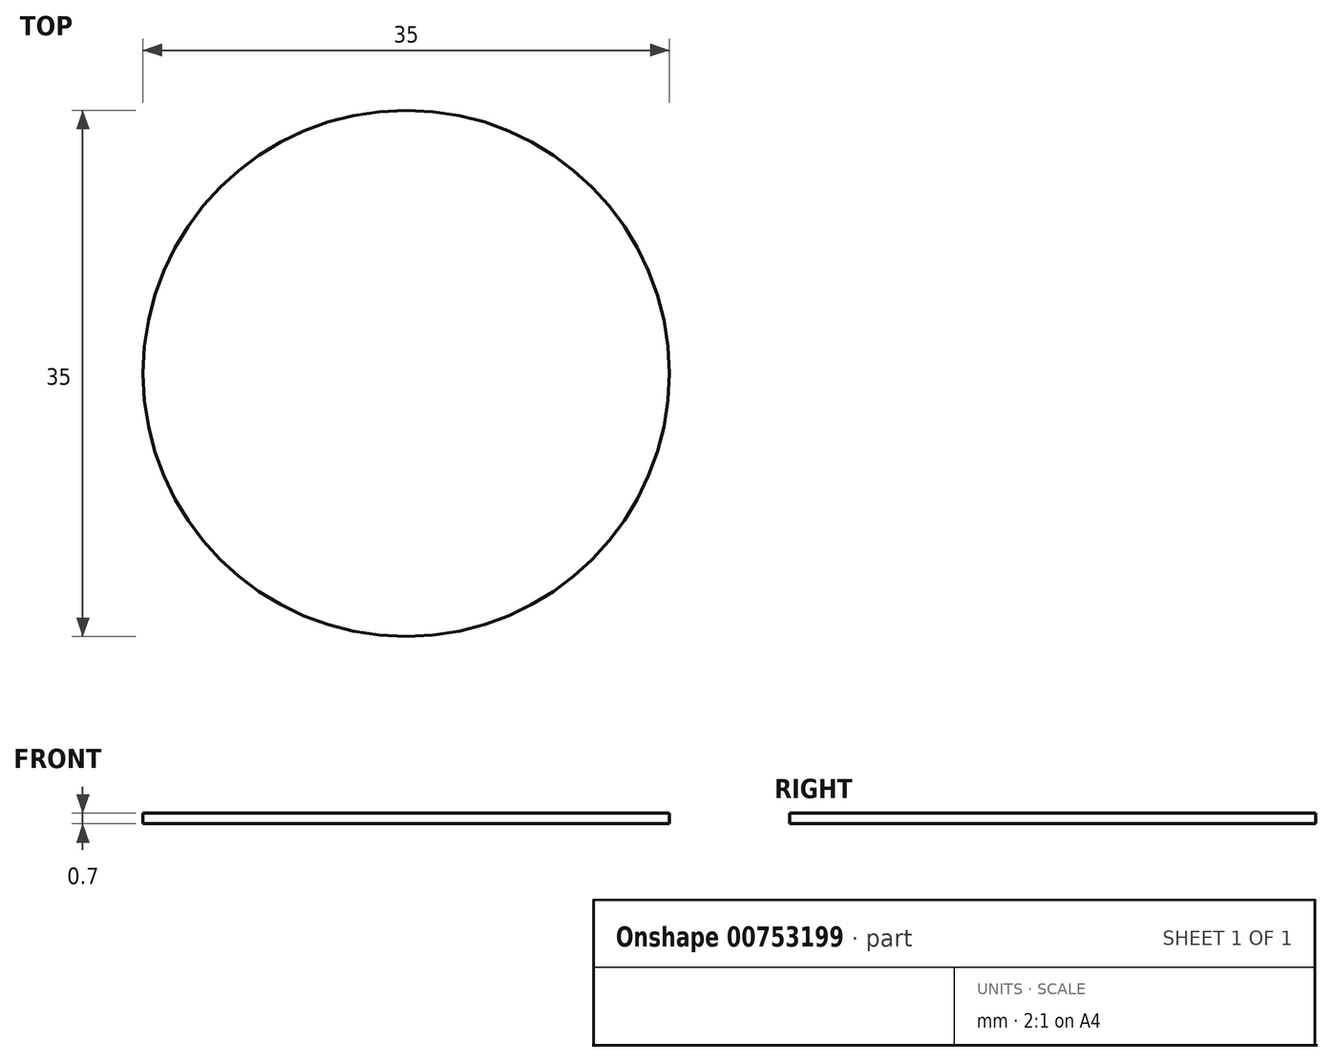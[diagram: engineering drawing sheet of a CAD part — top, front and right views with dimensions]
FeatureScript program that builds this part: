
annotation { "Feature Type Name" : "Feature", "Feature Type Description" : "" }
export const myFeature = defineFeature(function(context is Context, id is Id, definition is map)
    precondition{}
    {
        {
            var Q0;
            Q0=qCreatedBy(makeId("Top.planeOp"),FACE);
            var sketch = newSketch(context, id + "F0", { "sketchPlane" : qUnion([Q0])});
            skCircle(sketch, "E0", {"center": v(0, 0) * mm, "radius": 17.5 * mm});
            skSolve(sketch);
        }
        {
            var Q0;
            Q0 = qSketchRegion(id + "F0", true);
            extrude(context, id + "F1", {"entities" : qUnion([Q0]), "depth" : 0.7 * mm, "offsetDistance" : 25 * mm});
        }
    });
